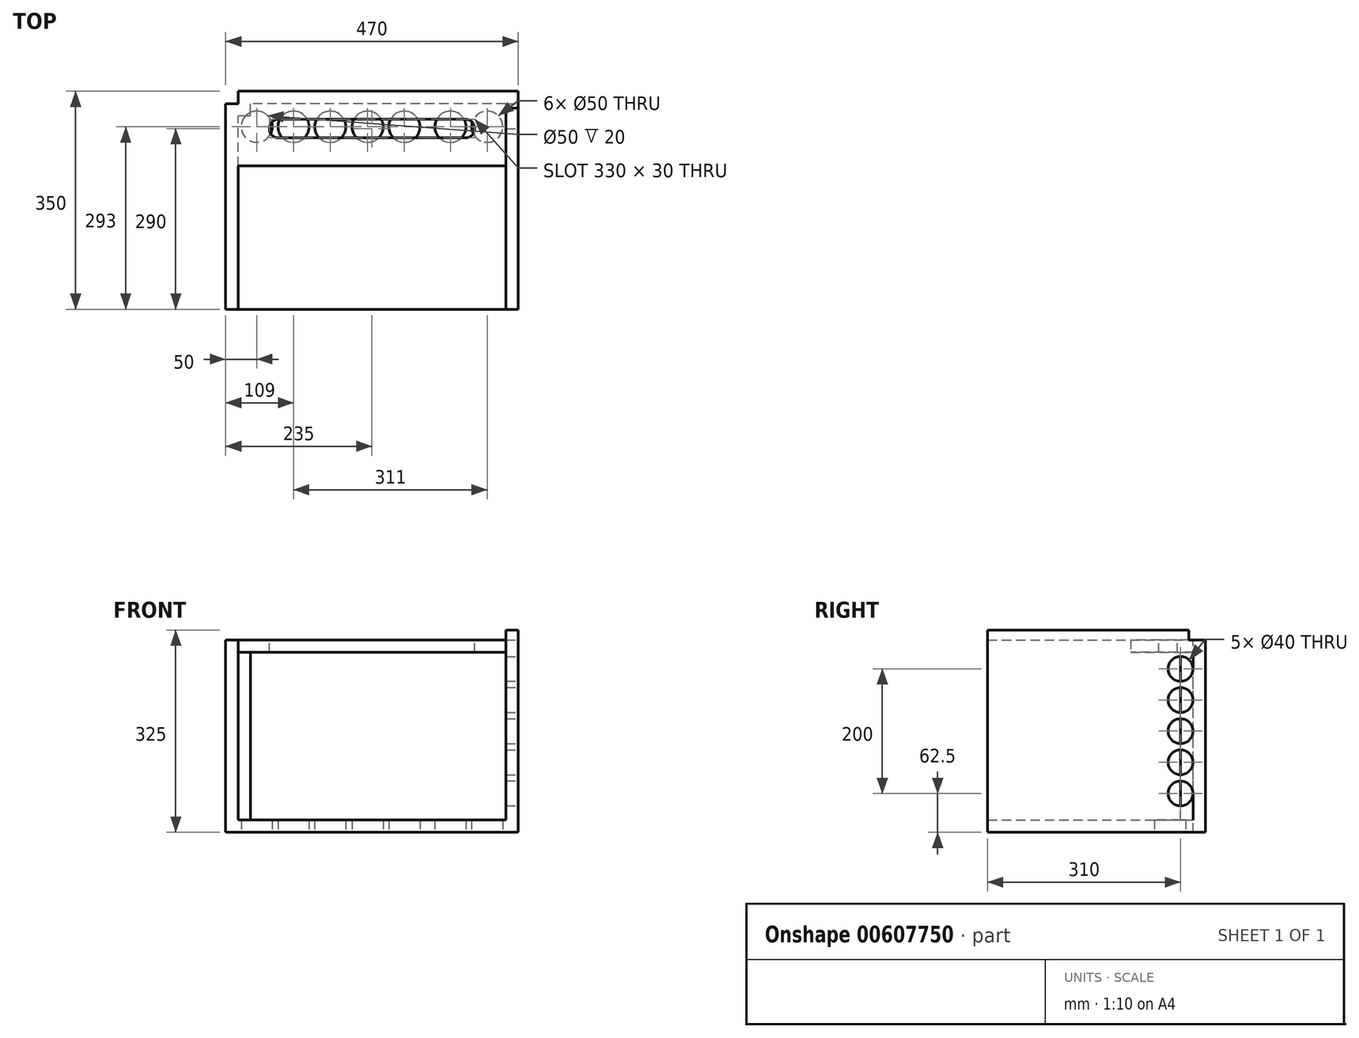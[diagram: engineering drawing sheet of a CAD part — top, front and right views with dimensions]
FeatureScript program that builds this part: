
annotation { "Feature Type Name" : "Feature", "Feature Type Description" : "" }
export const myFeature = defineFeature(function(context is Context, id is Id, definition is map)
    precondition{}
    {
        {
            var Q0;
            Q0=qCreatedBy(makeId("Front.planeOp"),FACE);
            var sketch = newSketch(context, id + "F0", { "sketchPlane" : qUnion([Q0])});
            skLineSegment(sketch, "E0.bottom", {"start": v(0, 0) * mm, "end": v(470, 0) * mm});
            skLineSegment(sketch, "E0.top", {"start": v(0, 325) * mm, "end": v(470, 325) * mm});
            skLineSegment(sketch, "E0.left", {"start": v(0, 0) * mm, "end": v(0, 325) * mm});
            skLineSegment(sketch, "E0.right", {"start": v(470, 0) * mm, "end": v(470, 325) * mm});
            skSolve(sketch);
        }
        {
            var Q0;
            Q0 = qSketchRegion(id + "F0", true);
            extrude(context, id + "F1", {"entities" : qUnion([Q0]), "depth" : 350 * mm, "offsetDistance" : 25 * mm});
        }
        {
            var Q0;
            Q0=makeQuery(id+"F1.opExtrude","CAP_FACE",FACE,{"disambiguationData":[OSD([sQuery(id+"F0.wireOp",EDGE,"E0.bottom"),sQuery(id+"F0.wireOp",EDGE,"E0.top"),sQuery(id+"F0.wireOp",EDGE,"E0.left"),sQuery(id+"F0.wireOp",EDGE,"E0.right")])],"isStart":false});
            var Q1;
            Q1=makeQuery(id+"F1.opExtrude","SWEPT_FACE",FACE,{"disambiguationData":[OSD([sQuery(id+"F0.wireOp",EDGE,"E0.top")])]});
            shell(context, id + "F2", {"entities" : qUnion([Q0, Q1]), "thickness" : 20 * mm});
        }
        {
            var Q0;
            Q0=makeQuery(id+"F1.opExtrude","SWEPT_FACE",FACE,{"disambiguationData":[OSD([sQuery(id+"F0.wireOp",EDGE,"E0.right")])]});
            var sketch = newSketch(context, id + "F3", { "sketchPlane" : qUnion([Q0])});
            skLineSegment(sketch, "E1.bottom", {"start": v(0, 325) * mm, "end": v(-27, 325) * mm});
            skLineSegment(sketch, "E1.top", {"start": v(0, 309) * mm, "end": v(-27, 309) * mm});
            skLineSegment(sketch, "E1.left", {"start": v(0, 325) * mm, "end": v(0, 309) * mm});
            skLineSegment(sketch, "E1.right", {"start": v(-27, 325) * mm, "end": v(-27, 309) * mm});
            skSolve(sketch);
        }
        {
            var Q0;
            Q0 = qSketchRegion(id + "F3", true);
            extrude(context, id + "F4", {"entities" : qUnion([Q0]), "operationType" : NewBodyOperationType.REMOVE, "endBound" : BoundingType.THROUGH_ALL, "oppositeDirection" : true, "depth" : 25 * mm, "offsetDistance" : 25 * mm});
        }
        {
            var Q0;
            Q0=qCreatedBy(makeId("Top.planeOp"),FACE);
            var sketch = newSketch(context, id + "F5", { "sketchPlane" : qUnion([Q0])});
            skCircle(sketch, "E2", {"center": v(50, -57) * mm, "radius": 25 * mm});
            skCircle(sketch, "E3", {"center": v(109, -57) * mm, "radius": 25 * mm});
            skCircle(sketch, "E4", {"center": v(168, -57) * mm, "radius": 25 * mm});
            skCircle(sketch, "E5", {"center": v(361, -57) * mm, "radius": 25 * mm});
            skCircle(sketch, "E6", {"center": v(420, -57) * mm, "radius": 25 * mm});
            skCircle(sketch, "E7", {"center": v(228, -57) * mm, "radius": 25 * mm});
            skCircle(sketch, "E8", {"center": v(287, -57) * mm, "radius": 25 * mm});
            skSolve(sketch);
        }
        {
            var Q0;
            Q0 = qSketchRegion(id + "F5", true);
            extrude(context, id + "F6", {"entities" : qUnion([Q0]), "operationType" : NewBodyOperationType.REMOVE, "endBound" : BoundingType.THROUGH_ALL, "depth" : 25 * mm, "offsetDistance" : 25 * mm});
        }
        {
            var Q0;
            Q0=makeQuery(id+"F1.opExtrude","SWEPT_FACE",FACE,{"disambiguationData":[OSD([sQuery(id+"F0.wireOp",EDGE,"E0.right")])]});
            var sketch = newSketch(context, id + "F7", { "sketchPlane" : qUnion([Q0])});
            skCircle(sketch, "E9", {"center": v(-40, 62.5) * mm, "radius": 20 * mm});
            skCircle(sketch, "E10", {"center": v(-40, 162.5) * mm, "radius": 20 * mm});
            skCircle(sketch, "E11", {"center": v(-40, 212.5) * mm, "radius": 20 * mm});
            skCircle(sketch, "E12", {"center": v(-40, 262.5) * mm, "radius": 20 * mm});
            skCircle(sketch, "E13", {"center": v(-40, 112.5) * mm, "radius": 20 * mm});
            skLineSegment(sketch, "E14", {"start": v(-40, 162.5) * mm, "end": v(-350, 162.5) * mm});
            skSolve(sketch);
        }
        {
            var Q0;
            Q0 = qSketchRegion(id + "F7", true);
            extrude(context, id + "F8", {"entities" : qUnion([Q0]), "operationType" : NewBodyOperationType.REMOVE, "endBound" : BoundingType.UP_TO_NEXT, "oppositeDirection" : true, "depth" : 25 * mm, "offsetDistance" : 25 * mm});
        }
        {
            var Q0;
            {var subQ0=sQuery(id+"F0.wireOp",EDGE,"E0.left");Q0=makeQuery(id+"F4.boolean.opBoolean","COPY",FACE,{"disambiguationData":[TD([makeQuery(id+"F1.opExtrude","SWEPT_FACE",FACE,{"disambiguationData":[OSD([subQ0])]})])],"derivedFrom":makeQuery(id+"F4.opExtrude","SWEPT_FACE",FACE,{"disambiguationData":[OSD([sQuery(id+"F3.wireOp",EDGE,"E1.right")])]})});}
            var sketch = newSketch(context, id + "F9", { "sketchPlane" : qUnion([Q0])});
            skLineSegment(sketch, "E15.bottom", {"start": v(-20, 325) * mm, "end": v(0, 325) * mm});
            skLineSegment(sketch, "E15.top", {"start": v(-20, 309) * mm, "end": v(0, 309) * mm});
            skLineSegment(sketch, "E15.left", {"start": v(-20, 325) * mm, "end": v(-20, 309) * mm});
            skLineSegment(sketch, "E15.right", {"start": v(0, 325) * mm, "end": v(0, 309) * mm});
            skSolve(sketch);
        }
        {
            var Q0;
            Q0 = qSketchRegion(id + "F9", true);
            extrude(context, id + "F10", {"entities" : qUnion([Q0]), "operationType" : NewBodyOperationType.REMOVE, "endBound" : BoundingType.THROUGH_ALL, "oppositeDirection" : true, "depth" : 25 * mm, "offsetDistance" : 25 * mm});
        }
        {
            var Q0;
            Q0=makeQuery(id+"F10.boolean.opBoolean","MERGE",FACE,{"derivedFrom":[makeQuery(id+"F4.boolean.opBoolean","COPY",FACE,{"derivedFrom":makeQuery(id+"F4.opExtrude","SWEPT_FACE",FACE,{"disambiguationData":[OSD([sQuery(id+"F3.wireOp",EDGE,"E1.top")])]})}),makeQuery(id+"F10.opExtrude","SWEPT_FACE",FACE,{"disambiguationData":[OSD([sQuery(id+"F9.wireOp",EDGE,"OAwPVCd2-2igP-ew8Y-YuX9-DXjRHMHebxop.top")])]})]});
            var sketch = newSketch(context, id + "F11", { "sketchPlane" : qUnion([Q0])});
            skLineSegment(sketch, "E16.bottom", {"start": v(20, -20) * mm, "end": v(40, -20) * mm});
            skLineSegment(sketch, "E16.top", {"start": v(20, -40) * mm, "end": v(40, -40) * mm});
            skLineSegment(sketch, "E16.left", {"start": v(20, -20) * mm, "end": v(20, -40) * mm});
            skLineSegment(sketch, "E16.right", {"start": v(40, -20) * mm, "end": v(40, -40) * mm});
            skSolve(sketch);
        }
        {
            var Q0;
            Q0 = qSketchRegion(id + "F11", true);
            var Q1;
            Q1=makeQuery(id+"F2.opShell","OFFSET_FACE",FACE,{"disambiguationData":[OSD([sQuery(id+"F0.wireOp",EDGE,"E0.bottom")])]});
            extrude(context, id + "F12", {"entities" : qUnion([Q0]), "operationType" : NewBodyOperationType.ADD, "endBound" : BoundingType.UP_TO_SURFACE, "oppositeDirection" : true, "depth" : 25 * mm, "endBoundEntityFace" : qUnion([Q1]), "offsetDistance" : 25 * mm});
        }
        {
            var Q0;
            Q0=makeQuery(id+"F12.boolean.opBoolean","MERGE",FACE,{"derivedFrom":[makeQuery(id+"F10.boolean.opBoolean","MERGE",FACE,{"derivedFrom":[makeQuery(id+"F4.boolean.opBoolean","COPY",FACE,{"derivedFrom":makeQuery(id+"F4.opExtrude","SWEPT_FACE",FACE,{"disambiguationData":[OSD([sQuery(id+"F3.wireOp",EDGE,"E1.top")])]})}),makeQuery(id+"F10.opExtrude","SWEPT_FACE",FACE,{"disambiguationData":[OSD([sQuery(id+"F9.wireOp",EDGE,"OAwPVCd2-2igP-ew8Y-YuX9-DXjRHMHebxop.top")])]})]}),makeQuery(id+"F12.opExtrude","CAP_FACE",FACE,{"disambiguationData":[OSD([sQuery(id+"F11.wireOp",EDGE,"aIlBuQSI-t0lO-PcRd-YrqE-GrSIx7AOgO1x.bottom"),sQuery(id+"F11.wireOp",EDGE,"aIlBuQSI-t0lO-PcRd-YrqE-GrSIx7AOgO1x.top"),sQuery(id+"F11.wireOp",EDGE,"aIlBuQSI-t0lO-PcRd-YrqE-GrSIx7AOgO1x.left"),sQuery(id+"F11.wireOp",EDGE,"aIlBuQSI-t0lO-PcRd-YrqE-GrSIx7AOgO1x.right")])],"isStart":true})]});
            var sketch = newSketch(context, id + "F13", { "sketchPlane" : qUnion([Q0])});
            skLineSegment(sketch, "E17.bottom", {"start": v(0, 0) * mm, "end": v(20, 0) * mm});
            skLineSegment(sketch, "E17.top", {"start": v(0, -20) * mm, "end": v(20, -20) * mm});
            skLineSegment(sketch, "E17.left", {"start": v(0, 0) * mm, "end": v(0, -20) * mm});
            skLineSegment(sketch, "E17.right", {"start": v(20, 0) * mm, "end": v(20, -20) * mm});
            skSolve(sketch);
        }
        {
            var Q0;
            Q0 = qSketchRegion(id + "F13", true);
            extrude(context, id + "F14", {"entities" : qUnion([Q0]), "operationType" : NewBodyOperationType.REMOVE, "endBound" : BoundingType.THROUGH_ALL, "oppositeDirection" : true, "depth" : 25 * mm, "offsetDistance" : 25 * mm});
        }
        {
            var Q0;
            Q0=makeQuery(id+"F2.opShell","OFFSET_FACE",FACE,{"disambiguationData":[OSD([sQuery(id+"F0.wireOp",EDGE,"E0.left")])]});
            var sketch = newSketch(context, id + "F15", { "sketchPlane" : qUnion([Q0])});
            skLineSegment(sketch, "E18.bottom", {"start": v(-120, 309) * mm, "end": v(-20, 309) * mm});
            skLineSegment(sketch, "E18.top", {"start": v(-120, 289) * mm, "end": v(-20, 289) * mm});
            skLineSegment(sketch, "E18.left", {"start": v(-120, 309) * mm, "end": v(-120, 289) * mm});
            skLineSegment(sketch, "E18.right", {"start": v(-20, 309) * mm, "end": v(-20, 289) * mm});
            skSolve(sketch);
        }
        {
            var Q0;
            Q0 = qSketchRegion(id + "F15", true);
            var Q1;
            Q1=makeQuery(id+"F2.opShell","OFFSET_FACE",FACE,{"disambiguationData":[OSD([sQuery(id+"F0.wireOp",EDGE,"E0.right")])]});
            extrude(context, id + "F16", {"entities" : qUnion([Q0]), "operationType" : NewBodyOperationType.ADD, "endBound" : BoundingType.UP_TO_SURFACE, "depth" : 25 * mm, "endBoundEntityFace" : qUnion([Q1]), "offsetDistance" : 25 * mm});
        }
        {
            var Q0;
            Q0=makeQuery(id+"F16.boolean.opBoolean","MERGE",FACE,{"derivedFrom":[makeQuery(id+"F12.boolean.opBoolean","MERGE",FACE,{"derivedFrom":[makeQuery(id+"F10.boolean.opBoolean","MERGE",FACE,{"derivedFrom":[makeQuery(id+"F4.boolean.opBoolean","COPY",FACE,{"derivedFrom":makeQuery(id+"F4.opExtrude","SWEPT_FACE",FACE,{"disambiguationData":[OSD([sQuery(id+"F3.wireOp",EDGE,"E1.top")])]})}),makeQuery(id+"F10.opExtrude","SWEPT_FACE",FACE,{"disambiguationData":[OSD([sQuery(id+"F9.wireOp",EDGE,"E15.top")])]})]}),makeQuery(id+"F12.opExtrude","CAP_FACE",FACE,{"disambiguationData":[OSD([sQuery(id+"F11.wireOp",EDGE,"E16.bottom"),sQuery(id+"F11.wireOp",EDGE,"E16.top"),sQuery(id+"F11.wireOp",EDGE,"E16.left"),sQuery(id+"F11.wireOp",EDGE,"E16.right")])],"isStart":true})]}),makeQuery(id+"F16.opExtrude","SWEPT_FACE",FACE,{"disambiguationData":[OSD([sQuery(id+"F15.wireOp",EDGE,"E18.bottom")])]})]});
            var sketch = newSketch(context, id + "F17", { "sketchPlane" : qUnion([Q0])});
            skLineSegment(sketch, "E19", {"start": v(85, -45) * mm, "end": v(385, -45) * mm});
            skLineSegment(sketch, "E20", {"start": v(85, -75) * mm, "end": v(385, -75) * mm});
            skArc(sketch, "E21", {"start": v(385, -75) * mm, "mid": v(400, -60) * mm, "end": v(385, -45) * mm});
            skArc(sketch, "E22", {"start": v(85, -45) * mm, "mid": v(70, -60) * mm, "end": v(85, -75) * mm});
            skLineSegment(sketch, "E23", {"start": v(235, -45) * mm, "end": v(235, -120) * mm});
            skLineSegment(sketch, "E24", {"start": v(85, -60) * mm, "end": v(85, 0) * mm});
            skLineSegment(sketch, "E25", {"start": v(85, -60) * mm, "end": v(85, -120) * mm});
            skSolve(sketch);
        }
        {
            var Q0;
            Q0 = qSketchRegion(id + "F17", true);
            var Q1;
            Q1=makeQuery(id+"F16.opExtrude","SWEPT_FACE",FACE,{"disambiguationData":[OSD([sQuery(id+"F15.wireOp",EDGE,"E18.top")])]});
            extrude(context, id + "F18", {"entities" : qUnion([Q0]), "operationType" : NewBodyOperationType.REMOVE, "endBound" : BoundingType.UP_TO_SURFACE, "oppositeDirection" : true, "depth" : 25 * mm, "endBoundEntityFace" : qUnion([Q1]), "offsetDistance" : 25 * mm});
        }
    });
